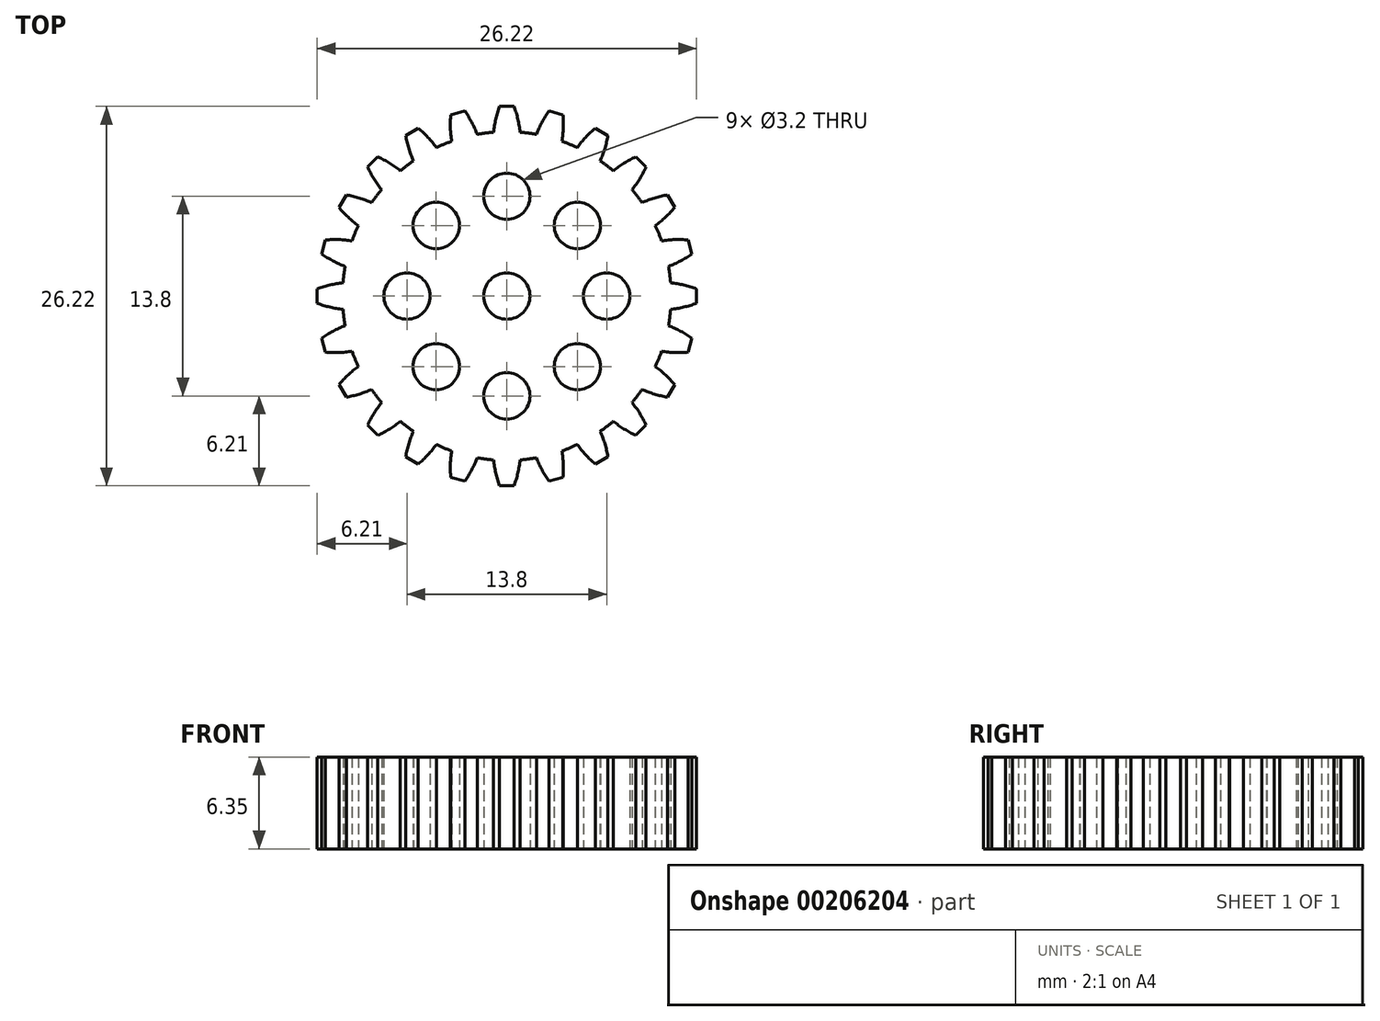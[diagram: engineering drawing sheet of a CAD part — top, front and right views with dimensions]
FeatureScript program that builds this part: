
annotation { "Feature Type Name" : "Feature", "Feature Type Description" : "" }
export const myFeature = defineFeature(function(context is Context, id is Id, definition is map)
    precondition{}
    {
        {
            var Q0;
            Q0=qCreatedBy(makeId("Top.planeOp"),FACE);
            var sketch = newSketch(context, id + "F0", { "sketchPlane" : qUnion([Q0])});
            skLineSegment(sketch, "E0", {"start": v(-0.5, 13.1) * mm, "end": v(0.5, 13.1) * mm});
            skArc(sketch, "E1", {"start": v(-0.5, 13.1) * mm, "mid": v(-0.76, 12.23) * mm, "end": v(-0.91, 11.32) * mm});
            skArc(sketch, "E2.MirrorCS", {"start": v(0.5, 13.1) * mm, "mid": v(0.76, 12.23) * mm, "end": v(0.91, 11.32) * mm});
            skCircle(sketch, "E3", {"center": v(0, 6.9) * mm, "radius": 1.6 * mm});
            skCircle(sketch, "E4.1.0", {"center": v(-4.88, 4.88) * mm, "radius": 1.6 * mm});
            skCircle(sketch, "E4.2.0", {"center": v(-6.9, 0) * mm, "radius": 1.6 * mm});
            skCircle(sketch, "E4.3.0", {"center": v(-4.88, -4.88) * mm, "radius": 1.6 * mm});
            skCircle(sketch, "E4.4.0", {"center": v(0, -6.9) * mm, "radius": 1.6 * mm});
            skCircle(sketch, "E4.5.0", {"center": v(4.88, -4.88) * mm, "radius": 1.6 * mm});
            skCircle(sketch, "E4.6.0", {"center": v(6.9, 0) * mm, "radius": 1.6 * mm});
            skCircle(sketch, "E4.7.0", {"center": v(4.88, 4.88) * mm, "radius": 1.6 * mm});
            skPoint(sketch, "E5.1.4", {"position": v(-0.5, 13.1) * mm});
            skArc(sketch, "E6", {"start": v(2.05, 11.18) * mm, "mid": v(1.48, 11.26) * mm, "end": v(0.91, 11.32) * mm});
            skPoint(sketch, "E7.orphan", {"position": v(2.9, 12.8) * mm});
            skPoint(sketch, "E8.orphan", {"position": v(0.94, 11) * mm});
            skPoint(sketch, "E9.orphan", {"position": v(-0.94, 11) * mm});
            skPoint(sketch, "E10.orphan", {"position": v(-2.9, 12.8) * mm});
            skArc(sketch, "E11.1.0", {"start": v(-0.91, 11.32) * mm, "mid": v(-1.48, 11.26) * mm, "end": v(-2.05, 11.18) * mm});
            skPoint(sketch, "E11.1.1", {"position": v(-3.88, 12.53) * mm});
            skArc(sketch, "E11.1.2", {"start": v(-3.88, 12.53) * mm, "mid": v(-3.9, 11.61) * mm, "end": v(-3.81, 10.7) * mm});
            skPoint(sketch, "E11.1.3", {"position": v(-3.75, 10.38) * mm});
            skArc(sketch, "E11.1.5", {"start": v(-2.9, 12.8) * mm, "mid": v(-2.43, 12.01) * mm, "end": v(-2.05, 11.18) * mm});
            skLineSegment(sketch, "E11.1.6", {"start": v(-3.88, 12.53) * mm, "end": v(-2.9, 12.8) * mm});
            skPoint(sketch, "E11.1.7", {"position": v(-1.94, 10.87) * mm});
            skArc(sketch, "E11.2.0", {"start": v(-3.81, 10.7) * mm, "mid": v(-4.35, 10.5) * mm, "end": v(-4.87, 10.26) * mm});
            skPoint(sketch, "E11.2.1", {"position": v(-6.99, 11.1) * mm});
            skArc(sketch, "E11.2.2", {"start": v(-6.99, 11.1) * mm, "mid": v(-6.78, 10.2) * mm, "end": v(-6.45, 9.35) * mm});
            skPoint(sketch, "E11.2.3", {"position": v(-6.31, 9.06) * mm});
            skPoint(sketch, "E11.2.4", {"position": v(-3.88, 12.53) * mm});
            skArc(sketch, "E11.2.5", {"start": v(-6.12, 11.6) * mm, "mid": v(-5.45, 10.97) * mm, "end": v(-4.87, 10.26) * mm});
            skLineSegment(sketch, "E11.2.6", {"start": v(-6.99, 11.1) * mm, "end": v(-6.12, 11.6) * mm});
            skPoint(sketch, "E11.2.7", {"position": v(-4.69, 10) * mm});
            skArc(sketch, "E11.3.0", {"start": v(-6.45, 9.35) * mm, "mid": v(-6.92, 9.01) * mm, "end": v(-7.36, 8.65) * mm});
            skPoint(sketch, "E11.3.1", {"position": v(-9.62, 8.91) * mm});
            skArc(sketch, "E11.3.2", {"start": v(-9.62, 8.91) * mm, "mid": v(-9.19, 8.1) * mm, "end": v(-8.65, 7.36) * mm});
            skPoint(sketch, "E11.3.3", {"position": v(-8.44, 7.11) * mm});
            skPoint(sketch, "E11.3.4", {"position": v(-6.99, 11.1) * mm});
            skArc(sketch, "E11.3.5", {"start": v(-8.91, 9.62) * mm, "mid": v(-8.1, 9.19) * mm, "end": v(-7.36, 8.65) * mm});
            skLineSegment(sketch, "E11.3.6", {"start": v(-9.62, 8.91) * mm, "end": v(-8.91, 9.62) * mm});
            skPoint(sketch, "E11.3.7", {"position": v(-7.11, 8.44) * mm});
            skArc(sketch, "E11.4.0", {"start": v(-8.65, 7.36) * mm, "mid": v(-9.01, 6.92) * mm, "end": v(-9.35, 6.45) * mm});
            skPoint(sketch, "E11.4.1", {"position": v(-11.6, 6.12) * mm});
            skArc(sketch, "E11.4.2", {"start": v(-11.6, 6.12) * mm, "mid": v(-10.97, 5.45) * mm, "end": v(-10.26, 4.87) * mm});
            skPoint(sketch, "E11.4.3", {"position": v(-10, 4.69) * mm});
            skPoint(sketch, "E11.4.4", {"position": v(-9.62, 8.91) * mm});
            skArc(sketch, "E11.4.5", {"start": v(-11.1, 6.99) * mm, "mid": v(-10.2, 6.78) * mm, "end": v(-9.35, 6.45) * mm});
            skLineSegment(sketch, "E11.4.6", {"start": v(-11.6, 6.12) * mm, "end": v(-11.1, 6.99) * mm});
            skPoint(sketch, "E11.4.7", {"position": v(-9.06, 6.31) * mm});
            skArc(sketch, "E11.5.0", {"start": v(-10.26, 4.87) * mm, "mid": v(-10.5, 4.35) * mm, "end": v(-10.7, 3.81) * mm});
            skPoint(sketch, "E11.5.1", {"position": v(-12.8, 2.9) * mm});
            skArc(sketch, "E11.5.2", {"start": v(-12.8, 2.9) * mm, "mid": v(-12.01, 2.43) * mm, "end": v(-11.18, 2.05) * mm});
            skPoint(sketch, "E11.5.3", {"position": v(-10.87, 1.94) * mm});
            skPoint(sketch, "E11.5.4", {"position": v(-11.6, 6.12) * mm});
            skArc(sketch, "E11.5.5", {"start": v(-12.53, 3.88) * mm, "mid": v(-11.61, 3.9) * mm, "end": v(-10.7, 3.81) * mm});
            skLineSegment(sketch, "E11.5.6", {"start": v(-12.8, 2.9) * mm, "end": v(-12.53, 3.88) * mm});
            skPoint(sketch, "E11.5.7", {"position": v(-10.38, 3.75) * mm});
            skArc(sketch, "E11.6.0", {"start": v(-11.18, 2.05) * mm, "mid": v(-11.26, 1.48) * mm, "end": v(-11.32, 0.91) * mm});
            skPoint(sketch, "E11.6.1", {"position": v(-13.1, -0.5) * mm});
            skArc(sketch, "E11.6.2", {"start": v(-13.1, -0.5) * mm, "mid": v(-12.23, -0.76) * mm, "end": v(-11.32, -0.91) * mm});
            skPoint(sketch, "E11.6.3", {"position": v(-11, -0.94) * mm});
            skPoint(sketch, "E11.6.4", {"position": v(-12.8, 2.9) * mm});
            skArc(sketch, "E11.6.5", {"start": v(-13.1, 0.5) * mm, "mid": v(-12.23, 0.76) * mm, "end": v(-11.32, 0.91) * mm});
            skLineSegment(sketch, "E11.6.6", {"start": v(-13.1, -0.5) * mm, "end": v(-13.1, 0.5) * mm});
            skPoint(sketch, "E11.6.7", {"position": v(-11, 0.94) * mm});
            skArc(sketch, "E11.7.0", {"start": v(-11.32, -0.91) * mm, "mid": v(-11.26, -1.48) * mm, "end": v(-11.18, -2.05) * mm});
            skPoint(sketch, "E11.7.1", {"position": v(-12.53, -3.88) * mm});
            skArc(sketch, "E11.7.2", {"start": v(-12.53, -3.88) * mm, "mid": v(-11.61, -3.9) * mm, "end": v(-10.7, -3.81) * mm});
            skPoint(sketch, "E11.7.3", {"position": v(-10.38, -3.75) * mm});
            skPoint(sketch, "E11.7.4", {"position": v(-13.1, -0.5) * mm});
            skArc(sketch, "E11.7.5", {"start": v(-12.8, -2.9) * mm, "mid": v(-12.01, -2.43) * mm, "end": v(-11.18, -2.05) * mm});
            skLineSegment(sketch, "E11.7.6", {"start": v(-12.53, -3.88) * mm, "end": v(-12.8, -2.9) * mm});
            skPoint(sketch, "E11.7.7", {"position": v(-10.87, -1.94) * mm});
            skArc(sketch, "E11.8.0", {"start": v(-10.7, -3.81) * mm, "mid": v(-10.5, -4.35) * mm, "end": v(-10.26, -4.87) * mm});
            skPoint(sketch, "E11.8.1", {"position": v(-11.1, -6.99) * mm});
            skArc(sketch, "E11.8.2", {"start": v(-11.1, -6.99) * mm, "mid": v(-10.2, -6.78) * mm, "end": v(-9.35, -6.45) * mm});
            skPoint(sketch, "E11.8.3", {"position": v(-9.06, -6.31) * mm});
            skPoint(sketch, "E11.8.4", {"position": v(-12.53, -3.88) * mm});
            skArc(sketch, "E11.8.5", {"start": v(-11.6, -6.12) * mm, "mid": v(-10.97, -5.45) * mm, "end": v(-10.26, -4.87) * mm});
            skLineSegment(sketch, "E11.8.6", {"start": v(-11.1, -6.99) * mm, "end": v(-11.6, -6.12) * mm});
            skPoint(sketch, "E11.8.7", {"position": v(-10, -4.69) * mm});
            skArc(sketch, "E11.9.0", {"start": v(-9.35, -6.45) * mm, "mid": v(-9.01, -6.92) * mm, "end": v(-8.65, -7.36) * mm});
            skPoint(sketch, "E11.9.1", {"position": v(-8.91, -9.62) * mm});
            skArc(sketch, "E11.9.2", {"start": v(-8.91, -9.62) * mm, "mid": v(-8.1, -9.19) * mm, "end": v(-7.36, -8.65) * mm});
            skPoint(sketch, "E11.9.3", {"position": v(-7.11, -8.44) * mm});
            skPoint(sketch, "E11.9.4", {"position": v(-11.1, -6.99) * mm});
            skArc(sketch, "E11.9.5", {"start": v(-9.62, -8.91) * mm, "mid": v(-9.19, -8.1) * mm, "end": v(-8.65, -7.36) * mm});
            skLineSegment(sketch, "E11.9.6", {"start": v(-8.91, -9.62) * mm, "end": v(-9.62, -8.91) * mm});
            skPoint(sketch, "E11.9.7", {"position": v(-8.44, -7.11) * mm});
            skArc(sketch, "E11.10.0", {"start": v(-7.36, -8.65) * mm, "mid": v(-6.92, -9.01) * mm, "end": v(-6.45, -9.35) * mm});
            skPoint(sketch, "E11.10.1", {"position": v(-6.12, -11.6) * mm});
            skArc(sketch, "E11.10.2", {"start": v(-6.12, -11.6) * mm, "mid": v(-5.45, -10.97) * mm, "end": v(-4.87, -10.26) * mm});
            skPoint(sketch, "E11.10.3", {"position": v(-4.69, -10) * mm});
            skPoint(sketch, "E11.10.4", {"position": v(-8.91, -9.62) * mm});
            skArc(sketch, "E11.10.5", {"start": v(-6.99, -11.1) * mm, "mid": v(-6.78, -10.2) * mm, "end": v(-6.45, -9.35) * mm});
            skLineSegment(sketch, "E11.10.6", {"start": v(-6.12, -11.6) * mm, "end": v(-6.99, -11.1) * mm});
            skPoint(sketch, "E11.10.7", {"position": v(-6.31, -9.06) * mm});
            skArc(sketch, "E11.11.0", {"start": v(-4.87, -10.26) * mm, "mid": v(-4.35, -10.5) * mm, "end": v(-3.81, -10.7) * mm});
            skPoint(sketch, "E11.11.1", {"position": v(-2.9, -12.8) * mm});
            skArc(sketch, "E11.11.2", {"start": v(-2.9, -12.8) * mm, "mid": v(-2.43, -12.01) * mm, "end": v(-2.05, -11.18) * mm});
            skPoint(sketch, "E11.11.3", {"position": v(-1.94, -10.87) * mm});
            skPoint(sketch, "E11.11.4", {"position": v(-6.12, -11.6) * mm});
            skArc(sketch, "E11.11.5", {"start": v(-3.88, -12.53) * mm, "mid": v(-3.9, -11.61) * mm, "end": v(-3.81, -10.7) * mm});
            skLineSegment(sketch, "E11.11.6", {"start": v(-2.9, -12.8) * mm, "end": v(-3.88, -12.53) * mm});
            skPoint(sketch, "E11.11.7", {"position": v(-3.75, -10.38) * mm});
            skArc(sketch, "E11.12.0", {"start": v(-2.05, -11.18) * mm, "mid": v(-1.48, -11.26) * mm, "end": v(-0.91, -11.32) * mm});
            skPoint(sketch, "E11.12.1", {"position": v(0.5, -13.1) * mm});
            skArc(sketch, "E11.12.2", {"start": v(0.5, -13.1) * mm, "mid": v(0.76, -12.23) * mm, "end": v(0.91, -11.32) * mm});
            skPoint(sketch, "E11.12.3", {"position": v(0.94, -11) * mm});
            skPoint(sketch, "E11.12.4", {"position": v(-2.9, -12.8) * mm});
            skArc(sketch, "E11.12.5", {"start": v(-0.5, -13.1) * mm, "mid": v(-0.76, -12.23) * mm, "end": v(-0.91, -11.32) * mm});
            skLineSegment(sketch, "E11.12.6", {"start": v(0.5, -13.1) * mm, "end": v(-0.5, -13.1) * mm});
            skPoint(sketch, "E11.12.7", {"position": v(-0.94, -11) * mm});
            skArc(sketch, "E11.13.0", {"start": v(0.91, -11.32) * mm, "mid": v(1.48, -11.26) * mm, "end": v(2.05, -11.18) * mm});
            skPoint(sketch, "E11.13.1", {"position": v(3.88, -12.53) * mm});
            skArc(sketch, "E11.13.2", {"start": v(3.88, -12.53) * mm, "mid": v(3.9, -11.61) * mm, "end": v(3.81, -10.7) * mm});
            skPoint(sketch, "E11.13.3", {"position": v(3.75, -10.38) * mm});
            skPoint(sketch, "E11.13.4", {"position": v(0.5, -13.1) * mm});
            skArc(sketch, "E11.13.5", {"start": v(2.9, -12.8) * mm, "mid": v(2.43, -12.01) * mm, "end": v(2.05, -11.18) * mm});
            skLineSegment(sketch, "E11.13.6", {"start": v(3.88, -12.53) * mm, "end": v(2.9, -12.8) * mm});
            skPoint(sketch, "E11.13.7", {"position": v(1.94, -10.87) * mm});
            skArc(sketch, "E11.14.0", {"start": v(3.81, -10.7) * mm, "mid": v(4.35, -10.5) * mm, "end": v(4.87, -10.26) * mm});
            skPoint(sketch, "E11.14.1", {"position": v(6.99, -11.1) * mm});
            skArc(sketch, "E11.14.2", {"start": v(6.99, -11.1) * mm, "mid": v(6.78, -10.2) * mm, "end": v(6.45, -9.35) * mm});
            skPoint(sketch, "E11.14.3", {"position": v(6.31, -9.06) * mm});
            skPoint(sketch, "E11.14.4", {"position": v(3.88, -12.53) * mm});
            skArc(sketch, "E11.14.5", {"start": v(6.12, -11.6) * mm, "mid": v(5.45, -10.97) * mm, "end": v(4.87, -10.26) * mm});
            skLineSegment(sketch, "E11.14.6", {"start": v(6.99, -11.1) * mm, "end": v(6.12, -11.6) * mm});
            skPoint(sketch, "E11.14.7", {"position": v(4.69, -10) * mm});
            skArc(sketch, "E11.15.0", {"start": v(6.45, -9.35) * mm, "mid": v(6.92, -9.01) * mm, "end": v(7.36, -8.65) * mm});
            skPoint(sketch, "E11.15.1", {"position": v(9.62, -8.91) * mm});
            skArc(sketch, "E11.15.2", {"start": v(9.62, -8.91) * mm, "mid": v(9.19, -8.1) * mm, "end": v(8.65, -7.36) * mm});
            skPoint(sketch, "E11.15.3", {"position": v(8.44, -7.11) * mm});
            skPoint(sketch, "E11.15.4", {"position": v(6.99, -11.1) * mm});
            skArc(sketch, "E11.15.5", {"start": v(8.91, -9.62) * mm, "mid": v(8.1, -9.19) * mm, "end": v(7.36, -8.65) * mm});
            skLineSegment(sketch, "E11.15.6", {"start": v(9.62, -8.91) * mm, "end": v(8.91, -9.62) * mm});
            skPoint(sketch, "E11.15.7", {"position": v(7.11, -8.44) * mm});
            skArc(sketch, "E11.16.0", {"start": v(8.65, -7.36) * mm, "mid": v(9.01, -6.92) * mm, "end": v(9.35, -6.45) * mm});
            skPoint(sketch, "E11.16.1", {"position": v(11.6, -6.12) * mm});
            skArc(sketch, "E11.16.2", {"start": v(11.6, -6.12) * mm, "mid": v(10.97, -5.45) * mm, "end": v(10.26, -4.87) * mm});
            skPoint(sketch, "E11.16.3", {"position": v(10, -4.69) * mm});
            skPoint(sketch, "E11.16.4", {"position": v(9.62, -8.91) * mm});
            skArc(sketch, "E11.16.5", {"start": v(11.1, -6.99) * mm, "mid": v(10.2, -6.78) * mm, "end": v(9.35, -6.45) * mm});
            skLineSegment(sketch, "E11.16.6", {"start": v(11.6, -6.12) * mm, "end": v(11.1, -6.99) * mm});
            skPoint(sketch, "E11.16.7", {"position": v(9.06, -6.31) * mm});
            skArc(sketch, "E11.17.0", {"start": v(10.26, -4.87) * mm, "mid": v(10.5, -4.35) * mm, "end": v(10.7, -3.81) * mm});
            skPoint(sketch, "E11.17.1", {"position": v(12.8, -2.9) * mm});
            skArc(sketch, "E11.17.2", {"start": v(12.8, -2.9) * mm, "mid": v(12.01, -2.43) * mm, "end": v(11.18, -2.05) * mm});
            skPoint(sketch, "E11.17.3", {"position": v(10.87, -1.94) * mm});
            skPoint(sketch, "E11.17.4", {"position": v(11.6, -6.12) * mm});
            skArc(sketch, "E11.17.5", {"start": v(12.53, -3.88) * mm, "mid": v(11.61, -3.9) * mm, "end": v(10.7, -3.81) * mm});
            skLineSegment(sketch, "E11.17.6", {"start": v(12.8, -2.9) * mm, "end": v(12.53, -3.88) * mm});
            skPoint(sketch, "E11.17.7", {"position": v(10.38, -3.75) * mm});
            skArc(sketch, "E11.18.0", {"start": v(11.18, -2.05) * mm, "mid": v(11.26, -1.48) * mm, "end": v(11.32, -0.91) * mm});
            skPoint(sketch, "E11.18.1", {"position": v(13.1, 0.5) * mm});
            skArc(sketch, "E11.18.2", {"start": v(13.1, 0.5) * mm, "mid": v(12.23, 0.76) * mm, "end": v(11.32, 0.91) * mm});
            skPoint(sketch, "E11.18.3", {"position": v(11, 0.94) * mm});
            skPoint(sketch, "E11.18.4", {"position": v(12.8, -2.9) * mm});
            skArc(sketch, "E11.18.5", {"start": v(13.1, -0.5) * mm, "mid": v(12.23, -0.76) * mm, "end": v(11.32, -0.91) * mm});
            skLineSegment(sketch, "E11.18.6", {"start": v(13.1, 0.5) * mm, "end": v(13.1, -0.5) * mm});
            skPoint(sketch, "E11.18.7", {"position": v(11, -0.94) * mm});
            skArc(sketch, "E11.19.0", {"start": v(11.32, 0.91) * mm, "mid": v(11.26, 1.48) * mm, "end": v(11.18, 2.05) * mm});
            skPoint(sketch, "E11.19.1", {"position": v(12.53, 3.88) * mm});
            skArc(sketch, "E11.19.2", {"start": v(12.53, 3.88) * mm, "mid": v(11.61, 3.9) * mm, "end": v(10.7, 3.81) * mm});
            skPoint(sketch, "E11.19.3", {"position": v(10.38, 3.75) * mm});
            skPoint(sketch, "E11.19.4", {"position": v(13.1, 0.5) * mm});
            skArc(sketch, "E11.19.5", {"start": v(12.8, 2.9) * mm, "mid": v(12.01, 2.43) * mm, "end": v(11.18, 2.05) * mm});
            skLineSegment(sketch, "E11.19.6", {"start": v(12.53, 3.88) * mm, "end": v(12.8, 2.9) * mm});
            skPoint(sketch, "E11.19.7", {"position": v(10.87, 1.94) * mm});
            skArc(sketch, "E11.20.0", {"start": v(10.7, 3.81) * mm, "mid": v(10.5, 4.35) * mm, "end": v(10.26, 4.87) * mm});
            skPoint(sketch, "E11.20.1", {"position": v(11.1, 6.99) * mm});
            skArc(sketch, "E11.20.2", {"start": v(11.1, 6.99) * mm, "mid": v(10.2, 6.78) * mm, "end": v(9.35, 6.45) * mm});
            skPoint(sketch, "E11.20.3", {"position": v(9.06, 6.31) * mm});
            skPoint(sketch, "E11.20.4", {"position": v(12.53, 3.88) * mm});
            skArc(sketch, "E11.20.5", {"start": v(11.6, 6.12) * mm, "mid": v(10.97, 5.45) * mm, "end": v(10.26, 4.87) * mm});
            skLineSegment(sketch, "E11.20.6", {"start": v(11.1, 6.99) * mm, "end": v(11.6, 6.12) * mm});
            skPoint(sketch, "E11.20.7", {"position": v(10, 4.69) * mm});
            skArc(sketch, "E11.21.0", {"start": v(9.35, 6.45) * mm, "mid": v(9.01, 6.92) * mm, "end": v(8.65, 7.36) * mm});
            skPoint(sketch, "E11.21.1", {"position": v(8.91, 9.62) * mm});
            skArc(sketch, "E11.21.2", {"start": v(8.91, 9.62) * mm, "mid": v(8.1, 9.19) * mm, "end": v(7.36, 8.65) * mm});
            skPoint(sketch, "E11.21.3", {"position": v(7.11, 8.44) * mm});
            skPoint(sketch, "E11.21.4", {"position": v(11.1, 6.99) * mm});
            skArc(sketch, "E11.21.5", {"start": v(9.62, 8.91) * mm, "mid": v(9.19, 8.1) * mm, "end": v(8.65, 7.36) * mm});
            skLineSegment(sketch, "E11.21.6", {"start": v(8.91, 9.62) * mm, "end": v(9.62, 8.91) * mm});
            skPoint(sketch, "E11.21.7", {"position": v(8.44, 7.11) * mm});
            skArc(sketch, "E11.22.0", {"start": v(7.36, 8.65) * mm, "mid": v(6.92, 9.01) * mm, "end": v(6.45, 9.35) * mm});
            skPoint(sketch, "E11.22.1", {"position": v(6.12, 11.6) * mm});
            skArc(sketch, "E11.22.2", {"start": v(6.12, 11.6) * mm, "mid": v(5.45, 10.97) * mm, "end": v(4.87, 10.26) * mm});
            skPoint(sketch, "E11.22.3", {"position": v(4.69, 10) * mm});
            skPoint(sketch, "E11.22.4", {"position": v(8.91, 9.62) * mm});
            skArc(sketch, "E11.22.5", {"start": v(6.99, 11.1) * mm, "mid": v(6.78, 10.2) * mm, "end": v(6.45, 9.35) * mm});
            skLineSegment(sketch, "E11.22.6", {"start": v(6.12, 11.6) * mm, "end": v(6.99, 11.1) * mm});
            skPoint(sketch, "E11.22.7", {"position": v(6.31, 9.06) * mm});
            skArc(sketch, "E11.23.0", {"start": v(4.87, 10.26) * mm, "mid": v(4.35, 10.5) * mm, "end": v(3.81, 10.7) * mm});
            skArc(sketch, "E11.23.2", {"start": v(2.9, 12.8) * mm, "mid": v(2.43, 12.01) * mm, "end": v(2.05, 11.18) * mm});
            skPoint(sketch, "E11.23.3", {"position": v(1.94, 10.87) * mm});
            skPoint(sketch, "E11.23.4", {"position": v(6.12, 11.6) * mm});
            skArc(sketch, "E11.23.5", {"start": v(3.88, 12.53) * mm, "mid": v(3.9, 11.61) * mm, "end": v(3.81, 10.7) * mm});
            skLineSegment(sketch, "E11.23.6", {"start": v(2.9, 12.8) * mm, "end": v(3.88, 12.53) * mm});
            skPoint(sketch, "E11.23.7", {"position": v(3.75, 10.38) * mm});
            skCircle(sketch, "E12", {"center": v(0, 0) * mm, "radius": 1.6 * mm});
            skSolve(sketch);
        }
        {
            var Q0;
            Q0=qSketchRegion(id+"F0",true);
            extrude(context, id + "F1", {"entities" : qUnion([Q0]), "depth" : 6.35 * mm});
        }
    });
